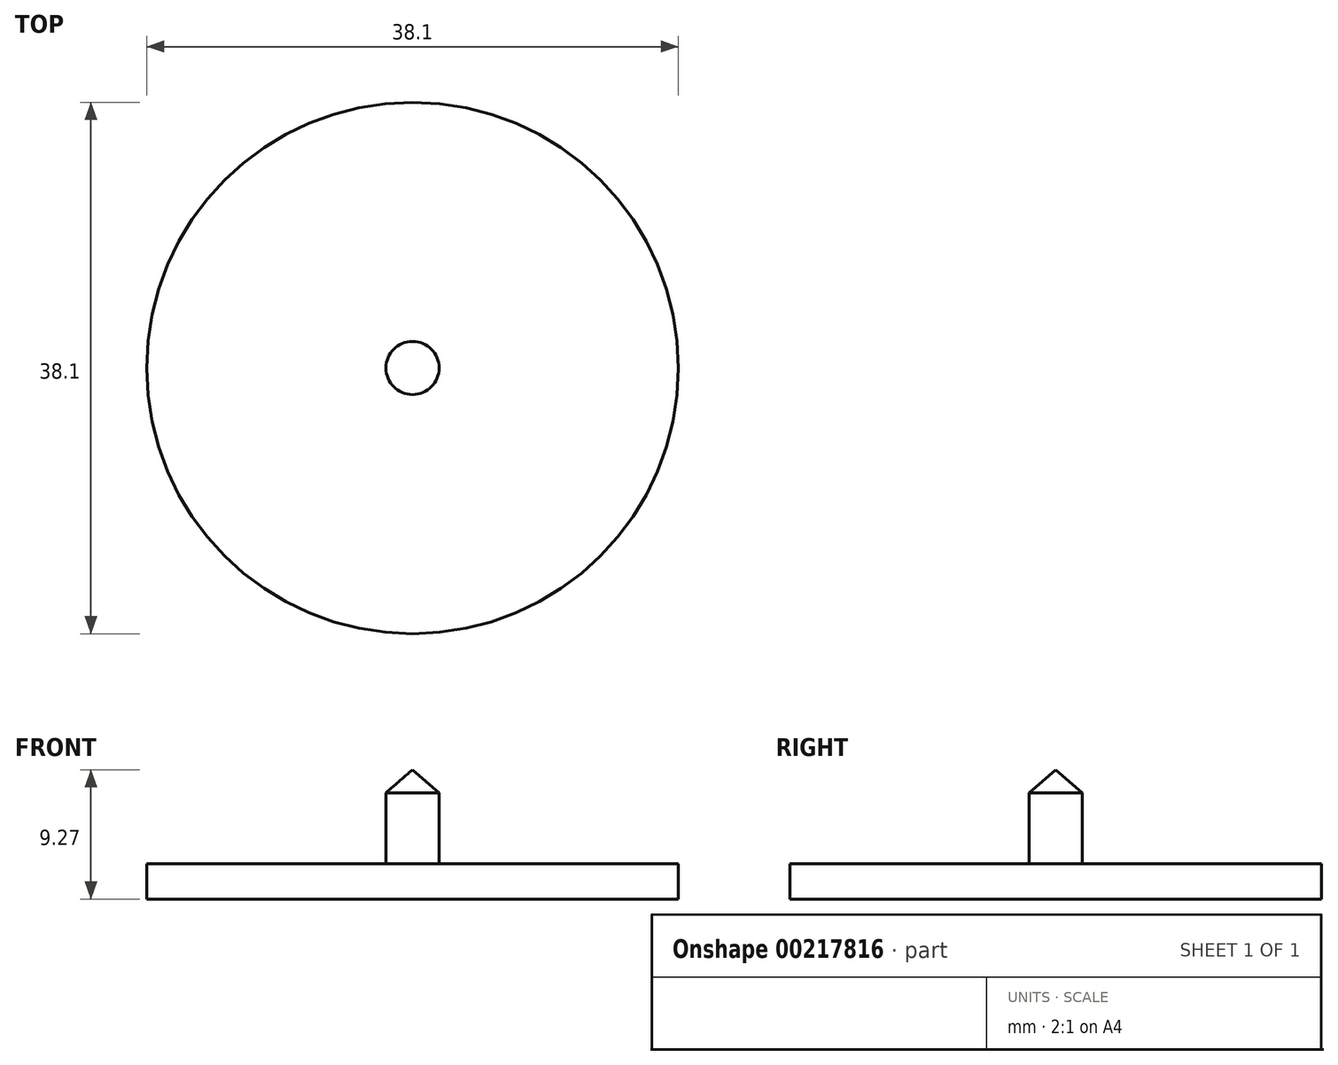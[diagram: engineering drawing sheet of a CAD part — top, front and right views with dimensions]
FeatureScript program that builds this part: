
annotation { "Feature Type Name" : "Feature", "Feature Type Description" : "" }
export const myFeature = defineFeature(function(context is Context, id is Id, definition is map)
    precondition{}
    {
        {
            var Q0;
            Q0=qCreatedBy(makeId("Front.planeOp"),FACE);
            var sketch = newSketch(context, id + "F0", { "sketchPlane" : qUnion([Q0])});
            skLineSegment(sketch, "E0.bottom", {"start": v(-19.05, 1.27) * mm, "end": v(19.05, 1.27) * mm});
            skLineSegment(sketch, "E0.top", {"start": v(-19.05, -1.27) * mm, "end": v(19.05, -1.27) * mm});
            skLineSegment(sketch, "E0.left", {"start": v(-19.05, 1.27) * mm, "end": v(-19.05, -1.27) * mm});
            skLineSegment(sketch, "E0.right", {"start": v(19.05, 1.27) * mm, "end": v(19.05, -1.27) * mm});
            skPoint(sketch, "E0.middle", {"position": v(0, 0) * mm});
            skLineSegment(sketch, "E1", {"start": v(-1.9, 1.27) * mm, "end": v(-1.9, 6.35) * mm});
            skLineSegment(sketch, "E2", {"start": v(-1.9, 6.35) * mm, "end": v(0, 8) * mm});
            skLineSegment(sketch, "E3", {"start": v(0, 15.15) * mm, "end": v(0, -13.24) * mm});
            skSolve(sketch);
        }
        {
            var Q0;
            {var subQ0=sQuery(id+"F0.wireOp",EDGE,"E1");Q0=makeQuery(id+"F0.imprint","IMPRINT",FACE,{"disambiguationData":[TD([[makeQuery(id+"F0.imprint","IMPRINT",EDGE,{"derivedFrom":subQ0}),-1.0]])]});}
            var Q1;
            {var subQ0=sQuery(id+"F0.wireOp",EDGE,"E0.left");Q1=makeQuery(id+"F0.imprint","IMPRINT",FACE,{"disambiguationData":[TD([[makeQuery(id+"F0.imprint","IMPRINT",EDGE,{"derivedFrom":subQ0}),1.0]])]});}
            var Q2;
            Q2=sQuery(id+"F0.wireOp",EDGE,"E3");
            revolve(context, id + "F1", {"entities" : qUnion([Q0, Q1]), "axis" : qUnion([Q2]), "revolveType" : RevolveType.FULL});
        }
    });
